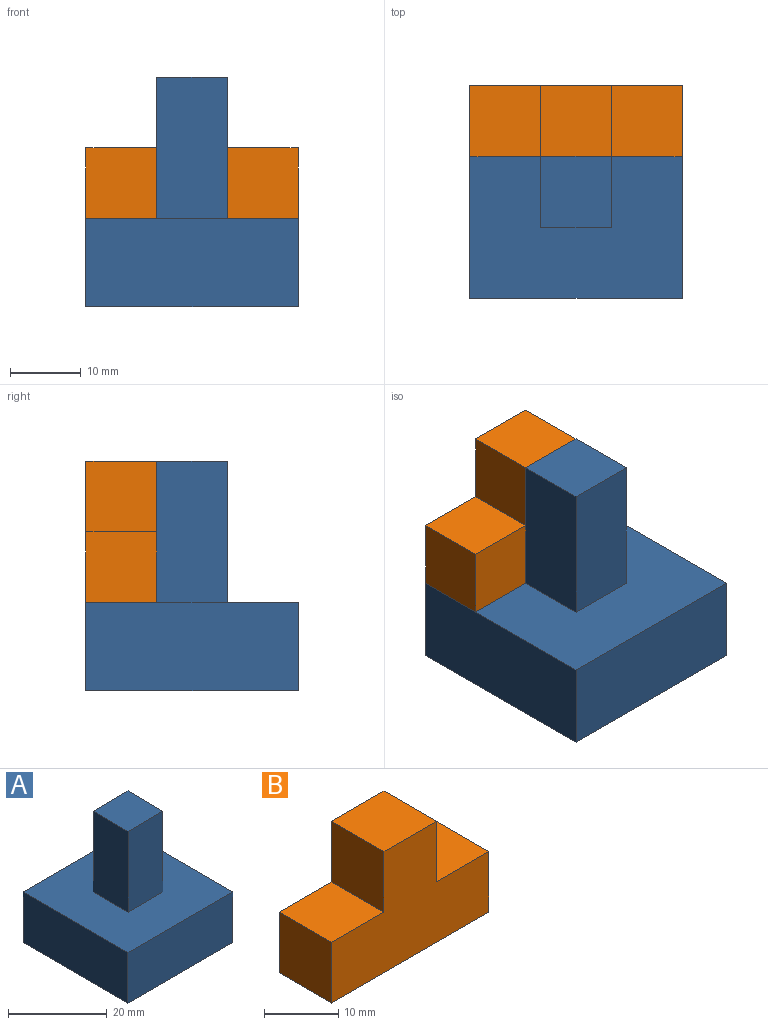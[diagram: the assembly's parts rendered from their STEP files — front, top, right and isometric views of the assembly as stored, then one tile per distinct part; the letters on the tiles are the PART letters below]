
ASSEMBLY  parts=2 mates=1
PART A: 74 faces, bbox 30x30x32.5 mm
  f0: plane 30x12.5mm, normal (0,1,0), area 375mm2, adj f1,f3,f4,f68
  f1: plane 30x12.5mm, normal (-1,0,0), area 375mm2, adj f0,f2,f4,f68
  f2: plane 30x12.5mm, normal (0,-1,0), area 375mm2, adj f1,f3,f4,f68
  f3: plane 30x12.5mm, normal (1,0,0), area 375mm2, adj f0,f2,f4,f68
  f4: plane 30x30mm, normal (0,0,1), area 800mm2, adj f0,f1,f2,f3,f5,f6,f7,f8
  f5: plane 20x10mm, normal (-1,0,0), area 200mm2, adj f4,f6,f8,f9
  f6: plane 20x10mm, normal (0,-1,0), area 200mm2, adj f4,f5,f7,f9
  f7: plane 20x10mm, normal (1,0,0), area 200mm2, adj f4,f6,f8,f9
  f8: plane 20x10mm, normal (0,1,0), area 200mm2, adj f4,f5,f7,f9
  f9: plane 10x10mm, normal (0,0,1), area 100mm2, adj f5,f6,f7,f8
  f10: plane 2.5x0.65mm, normal (0,-1,0), area 1.6mm2, adj f11,f67,f68,f69
  f11: plane 6.15x2.5mm, normal (0.93,-0.36,0), area 16.5mm2, adj f10,f12,f68,f69
  f12: plane 2.5x0.04mm, normal (0,-1,0), area 0.1mm2, adj f11,f13,f68,f69
  f13: extruded ~2.5x1.74mm, area 4.3mm2, adj f12,f14,f68,f69
  f14: plane 4.41x2.5mm, normal (-1,0,0), area 11mm2, adj f13,f15,f68,f69
  f15: plane 2.5x0.75mm, normal (0,-1,0), area 1.9mm2, adj f14,f16,f68,f69
  f16: plane 6.94x2.5mm, normal (1,0,0), area 17.4mm2, adj f15,f17,f68,f69
  f17: plane 2.5x1.22mm, normal (0,1,0), area 3mm2, adj f16,f18,f68,f69
  f18: plane 5.73x2.5mm, normal (-0.93,0.36,0), area 15.3mm2, adj f17,f19,f68,f69
  f19: plane 2.5x0.04mm, normal (0,1,0), area 0.1mm2, adj f18,f20,f68,f69
  f20: plane 5.73x2.5mm, normal (0.93,0.36,0), area 15.3mm2, adj f19,f21,f68,f69
  f21: plane 2.5x1.21mm, normal (0,1,0), area 3mm2, adj f20,f22,f68,f69
  f22: plane 6.94x2.5mm, normal (-1,0,0), area 17.4mm2, adj f21,f23,f68,f69
  f23: plane 2.5x0.81mm, normal (0,-1,0), area 2mm2, adj f22,f24,f68,f69
  f24: plane 4.47x2.5mm, normal (1,0,0), area 11.2mm2, adj f23,f25,f68,f69
  f25: extruded ~2.5x1.67mm, area 4.2mm2, adj f24,f26,f68,f69
  f26: plane 2.5x0.04mm, normal (0,-1,0), area 0.1mm2, adj f25,f67,f68,f69
  f27: plane 2.5x0.81mm, normal (0,-1,0), area 2mm2, adj f28,f63,f68,f73
  f28: plane 6.94x2.5mm, normal (1,0,0), area 17.4mm2, adj f27,f29,f68,f73
  f29: plane 2.5x0.81mm, normal (0,1,0), area 2mm2, adj f28,f63,f68,f73
  f30: extruded ~2.5x1.58mm, area 4.1mm2, adj f31,f64,f68,f72
  f31: extruded ~2.5x1.81mm, area 5.1mm2, adj f30,f32,f68,f72
  f32: extruded ~2.5x2.09mm, area 5.6mm2, adj f31,f33,f68,f72
  f33: extruded ~2.5x2.1mm, area 5.6mm2, adj f32,f34,f68,f72
  f34: extruded ~2.5x1.82mm, area 5.1mm2, adj f33,f35,f68,f72
  f35: extruded ~2.5x1.66mm, area 4.2mm2, adj f34,f36,f68,f72
  f36: plane 2.5x0.71mm, normal (-1,0,0), area 1.8mm2, adj f35,f37,f68,f72
  f37: extruded ~2.5x1.78mm, area 4.5mm2, adj f36,f38,f68,f72
  f38: extruded ~2.5x2.37mm, area 6.6mm2, adj f37,f39,f68,f72
  f39: extruded ~2.64x2.5mm, area 7.1mm2, adj f38,f40,f68,f72
  f40: extruded ~2.5x1.88mm, area 4.8mm2, adj f39,f41,f68,f72
  f41: extruded ~2.5x1.24mm, area 4.3mm2, adj f40,f42,f68,f72
  f42: extruded ~2.5x1.78mm, area 4.6mm2, adj f41,f43,f68,f72
  f43: extruded ~2.5x1.91mm, area 4.9mm2, adj f42,f64,f68,f72
  f44: plane 3.93x2.9mm, normal (-0.8,0.59,0), area 12.2mm2, adj f45,f65,f68,f71
  f45: plane 2.5x0.95mm, normal (0,-1,0), area 2.4mm2, adj f44,f46,f68,f71
  f46: plane 3.37x2.53mm, normal (0.8,-0.6,0), area 10.5mm2, adj f45,f47,f68,f71
  f47: plane 2.5x0.73mm, normal (-0.66,-0.75,0), area 2.4mm2, adj f46,f48,f68,f71
  f48: plane 2.72x2.5mm, normal (-1,0,0), area 6.8mm2, adj f47,f49,f68,f71
  f49: plane 2.5x0.81mm, normal (0,-1,0), area 2mm2, adj f48,f50,f68,f71
  f50: plane 6.94x2.5mm, normal (1,0,0), area 17.4mm2, adj f49,f51,f68,f71
  f51: plane 2.5x0.81mm, normal (0,1,0), area 2mm2, adj f50,f52,f68,f71
  f52: plane 3.44x2.5mm, normal (-1,0,0), area 8.6mm2, adj f51,f53,f68,f71
  f53: plane 3.44x3.15mm, normal (0.74,0.67,0), area 11.7mm2, adj f52,f54,f68,f71
  f54: plane 2.5x0.95mm, normal (0,1,0), area 2.4mm2, adj f53,f65,f68,f71
  f55: plane 3.47x2.5mm, normal (-0.88,0.47,0), area 9.8mm2, adj f56,f66,f68,f70
  f56: plane 3.47x2.5mm, normal (0.88,0.47,0), area 9.8mm2, adj f55,f57,f68,f70
  f57: plane 2.5x0.87mm, normal (0,1,0), area 2.2mm2, adj f56,f58,f68,f70
  f58: plane 4.25x2.5mm, normal (-0.88,-0.48,0), area 12.1mm2, adj f57,f59,f68,f70
  f59: plane 2.69x2.5mm, normal (-1,0,0), area 6.7mm2, adj f58,f60,f68,f70
  f60: plane 2.5x0.82mm, normal (0,-1,0), area 2mm2, adj f59,f61,f68,f70
  f61: plane 2.65x2.5mm, normal (1,0,0), area 6.6mm2, adj f60,f62,f68,f70
  f62: plane 4.29x2.5mm, normal (0.88,-0.47,0), area 12.2mm2, adj f61,f66,f68,f70
  f63: plane 6.94x2.5mm, normal (-1,0,0), area 17.4mm2, adj f27,f29,f68,f73
  f64: plane 2.5x0.69mm, normal (-0.9,-0.44,0), area 1.9mm2, adj f30,f43,f68,f72
  f65: plane 3.02x2.79mm, normal (-0.73,-0.68,0), area 10.3mm2, adj f44,f54,f68,f71
  f66: plane 2.5x0.88mm, normal (0,1,0), area 2.2mm2, adj f55,f62,f68,f70
  f67: plane 6.14x2.5mm, normal (-0.93,-0.36,0), area 16.5mm2, adj f10,f26,f68,f69
  f68: plane 30x30mm, normal (0,0,-1), area 841.4mm2, adj f0,f1,f2,f3,f10,f11,f12,f13
  f69: plane 6.94x6.87mm, normal (0,0,-1), area 20.6mm2, adj f10,f11,f12,f13,f14,f15,f16,f17
  f70: plane 6.94x5.44mm, normal (0,0,-1), area 9.1mm2, adj f55,f56,f57,f58,f59,f60,f61,f62
  f71: plane 6.94x5.01mm, normal (0,0,-1), area 12.7mm2, adj f44,f45,f46,f47,f48,f49,f50,f51
  f72: plane 7.14x5.25mm, normal (0,0,-1), area 10.5mm2, adj f30,f31,f32,f33,f34,f35,f36,f37
  f73: plane 6.94x0.81mm, normal (0,0,-1), area 5.6mm2, adj f27,f28,f29,f63
PART B: 10 faces, bbox 30x10x20 mm
  f0: plane 10x10mm, normal (0,0,1), area 100mm2, adj f1,f7,f8,f9
  f1: plane 10x10mm, normal (-1,0,0), area 100mm2, adj f0,f2,f8,f9
  f2: plane 10x10mm, normal (0,0,1), area 100mm2, adj f1,f3,f8,f9
  f3: plane 10x10mm, normal (-1,0,0), area 100mm2, adj f2,f4,f8,f9
  f4: plane 30x10mm, normal (0,0,-1), area 300mm2, adj f3,f5,f8,f9
  f5: plane 10x10mm, normal (1,0,0), area 100mm2, adj f4,f6,f8,f9
  f6: plane 10x10mm, normal (0,0,1), area 100mm2, adj f5,f7,f8,f9
  f7: plane 10x10mm, normal (1,0,0), area 100mm2, adj f0,f6,f8,f9
  f8: plane 30x20mm, normal (0,-1,0), area 400mm2, adj f0,f1,f2,f3,f4,f5,f6,f7
  f9: plane 30x20mm, normal (0,1,0), area 400mm2, adj f0,f1,f2,f3,f4,f5,f6,f7
PLACE A t=(-4.97,13.79,-12.22)mm
PLACE B t=(3.84,16.56,-2.39)mm
MATE fastened B.f8 <-> A.f8  axis (0,-1,0) through (0.93,6.56,-2.22)mm
